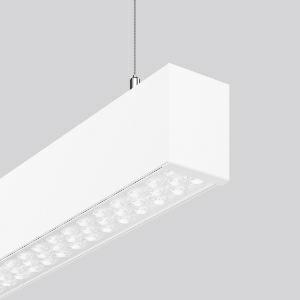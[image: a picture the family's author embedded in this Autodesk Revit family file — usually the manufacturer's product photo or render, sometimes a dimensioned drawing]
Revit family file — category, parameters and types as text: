
# Revit family: linedo_single_ip20_312564_002_1b1a
name_source: partatom
category: Lighting Fixtures
units: mm (PartAtom-declared; Revit-internal decimal feet)

## family parameters
Cut with Voids When Loaded = No
Host = Face
Light Source = No
Part Type = Normal
Room Calculation Point = No
Round Connector Dimension = Use Diameter
Shared = No

## types (1)
- LINEDO single IP20 (1 x LED Modul 830, 6100 lm, 3000)
    Apparent Load = 40 VA
    CIE Flux Codes = 86 96 99 100 100
    Color Rendering = 80
    Color Temperature = 3000
    Default Elevation = 1800 mm
    Description = Series: LINEDO single IP20
Stylish pendant luminaire. Housing: extruded aluminium profile, powder-coated. End cap aluminium powder-coated, without visible screws. High-efficiency LED units with optimum light control thanks to clear plastic (PC) lens optics. 2-point steel cable suspension freely positionable and infinitely height-adjustable. With power cord (2.5 m). Please order canopy separately if required. Perfect for office areas (RUG < 19) and environments with computer screens in accordance with EN 12464-1. 
Colour: traffic white, matt (RAL 9016)
Length: 2264 mm
Width: 58 mm
Height: 76 mm
Suspension length: 100-1500 mm
Lamp: LED
Socket: without socket
Colour temperature: 3000K
Colour rendering index (CRI): 80
System power: 40 W
Rated luminous flux: 6100 lm
Beam angle Down: 59°
Luminous efficiency: 153 lm/W
Control gear: Regulated power supply
Protection class: I
Type of protection: IP 20
    Height = 76 mm
    Lamp = 1 x LED Modul 830
    Lamp Light Flux = 6100 lm
    Lamp count = 1
    Length = 2264 mm
    Lifetime = 50000 h
    Luminous efficacy = 153 lm/W
    Manufacturer = RZB
    ModVariant = No
    Model = 312564.002
    Mounting Place = Ceiling
    Mounting Type = Surface mounted, Pendant
    Number of Poles = 1
    OnlyDefault = Yes
    Power Factor = 1
    Product Name = LINEDO single IP20
    Product group = Pendant luminaires
    ProductGroupID = 902
    Protection Class = Protection class I
    Protection Degree = IP 20
    RLX_Detail_Level = 1
    RLX_Emergency_Light_Flux = 0 lm
    RLX_Emergency_Type = 0
    RLX_Emergency_Type_DB = No
    RlxData = <blob elided: 24289 chars, md5=eff7812a>
    Socket = socket
    Standby Power = 0 W
    System Light Flux = 6100 lm
    System Power = 40 W
    Type Comments = ALEA SPOT
    Type Image = 312563.002.jpg
    URL = http://relux.com
    VarID = ---
    Voltage = 230 V
    Voltage Range = 220-240 V
    Weight = 0.00 kg
    Width = 58 mm

## geometry (parser evidence)
native form markers: Blend x4, Sweep x10
no freeform markers — native parametric forms only
